# Revit family: QF_CAPIC_CELTIC_W382221
name_source: partatom
category: Equipement spécialisé
revit_build: Autodesk Revit 2018 (Build: 20170223_1515(x64)
units: mm (PartAtom-declared; Revit-internal decimal feet)

## family parameters
Basée sur le plan de construction = Non
Cote de connecteur circulaire = Utiliser le diamètre
Couper avec des vides une fois chargée = Non
Numéro OmniClass = 23.40.40.14
Partagée = Non
Point de calcul de pièce = Non
Titre OmniClass = Food Service Equipment
Toujours verticalement = Oui
Type d'élément = Normal

## types (2) — shared parameters
Classification  Omniclass nombre et titre = 23.40.40.14
Diamètre de Raccordement Eau Adoucie = 0 mm
Diamètre de Raccordement Eau Chaude = 0 mm
Diamètre de Raccordement Eau Froide = 0 mm
Diamètre de Raccordement Evacuation = 0 mm
Diamètre de Raccordement Gaz = 0 mm
Débit Eau Adoucie = 0.0 L/s
Débit Eau Chaude = 0.0 L/s
Débit Eau Froide = 0.0 L/s
Débit Gaz = 0.0 L/s
Débit d'air d'extraction = 0.0 m³/h
Fabricant = CAPIC
Hauteur hors tout = 1015 mm  [stored 3.33005 ft]
Intensité nominale = 0 A
Longueur hors tout = 400 mm  [stored 1.31234 ft]
Modèle = W382221
Poids net à vide = 74.00 kg
Pression Maximum Eau Adoucie = 0.0 Pa
Profondeur hors tout = 835 mm
URL catalogue = http://www.capic-fr.com
zero-valued in all types: Hauteur de Raccordement Eau Adoucie du Sol Finis, Hauteur de Raccordement Eau Chaude du Sol Finis, Hauteur de Raccordement Eau Froide du Sol Finis, Hauteur de Raccordement Evacuation Directe du Sol Finis, Hauteur de Raccordement Gaz du Sol Finis, Puissance Gaz kW

## per-type parameters (varying)
| type | Description | Fréquence | Hauteur de Raccordement du Sol Finis | Phase | Puissance électrique  | Rampe IR (option X382210) | Tension |
| 400 x 835 x 900 mm | meuble salage neutre - placard ouevrt | 0 Hz | 0 mm  [stored 0 ft] | 0 | 0 W | Non | 0 V |
| 400 x 835 x 900 mm + RampeIR x382210 | meuble salage neutre + rampe IR- placard ouevrt | 50 Hz | 700 mm  [stored 2.29659 ft] | 1 | 1000 W | Oui | 230 V |

note: [stored X ft] marks values corroborated as IEEE doubles in the binary element streams (Revit-internal decimal feet)
